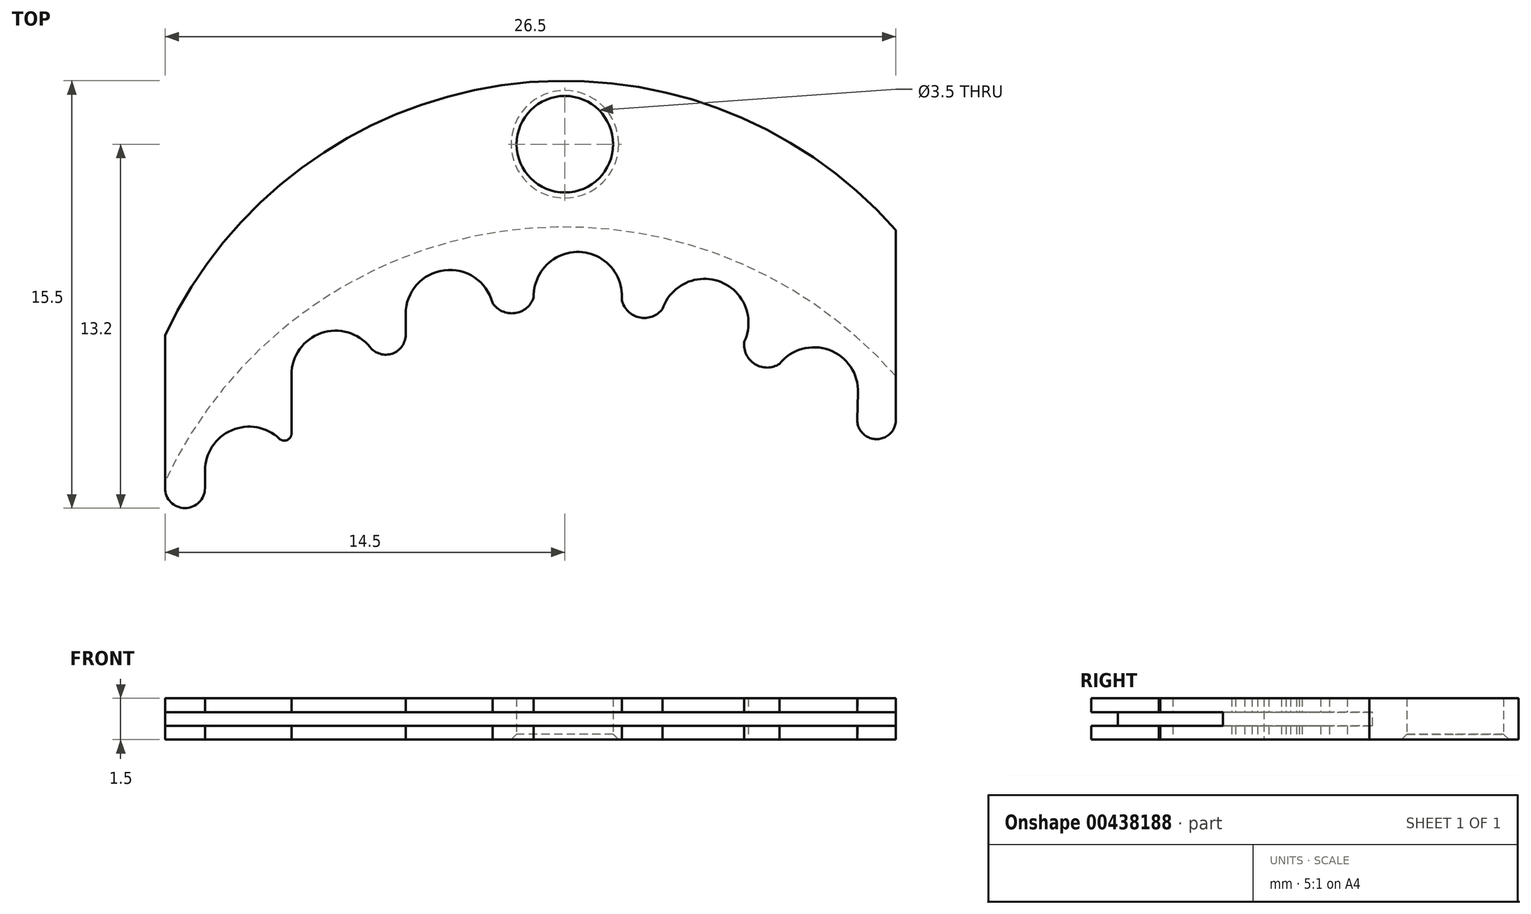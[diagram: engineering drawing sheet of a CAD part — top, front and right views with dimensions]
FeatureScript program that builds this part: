
annotation { "Feature Type Name" : "Feature", "Feature Type Description" : "" }
export const myFeature = defineFeature(function(context is Context, id is Id, definition is map)
    precondition{}
    {
        {
            var Q0;
            Q0=qCreatedBy(makeId("Top.planeOp"),FACE);
            var sketch = newSketch(context, id + "F0", { "sketchPlane" : qUnion([Q0])});
            skCircle(sketch, "E0", {"center": v(0, 0) * mm, "radius": 13 * mm, "construction": true});
            skCircle(sketch, "E1", {"center": v(0, 0) * mm, "radius": 13.5 * mm, "construction": true});
            skCircle(sketch, "E2", {"center": v(0, 0) * mm, "radius": 16 * mm, "construction": true});
            skLineSegment(sketch, "E3", {"start": v(0, 0) * mm, "end": v(0.47, 13.5) * mm, "construction": true});
            skLineSegment(sketch, "E4", {"start": v(0, 0) * mm, "end": v(5.06, 12.52) * mm, "construction": true});
            skLineSegment(sketch, "E5", {"start": v(0, 0) * mm, "end": v(9.03, 10.03) * mm, "construction": true});
            skLineSegment(sketch, "E6", {"start": v(0, 0) * mm, "end": v(-4.17, 12.84) * mm, "construction": true});
            skLineSegment(sketch, "E7", {"start": v(0, 0) * mm, "end": v(-8.31, 10.64) * mm, "construction": true});
            skLineSegment(sketch, "E8", {"start": v(0, 0) * mm, "end": v(-11.45, 7.15) * mm, "construction": true});
            skArc(sketch, "E9", {"start": v(2.06, 13.34) * mm, "mid": v(0.53, 15.1) * mm, "end": v(-1.13, 13.45) * mm});
            skArc(sketch, "E10", {"start": v(6.5, 11.83) * mm, "mid": v(5.66, 14) * mm, "end": v(3.54, 13.03) * mm});
            skArc(sketch, "E11", {"start": v(10.63, 9.98) * mm, "mid": v(9.59, 11.53) * mm, "end": v(7.78, 11.03) * mm});
            skArc(sketch, "E12", {"start": v(-2.62, 13.24) * mm, "mid": v(-4.38, 14.43) * mm, "end": v(-5.77, 12.84) * mm});
            skArc(sketch, "E13", {"start": v(-7, 11.55) * mm, "mid": v(-8.79, 12.17) * mm, "end": v(-9.91, 10.64) * mm});
            skArc(sketch, "E14", {"start": v(-10.35, 8.32) * mm, "mid": v(-12.08, 8.62) * mm, "end": v(-13.05, 7.15) * mm});
            skArc(sketch, "E15", {"start": v(-2.62, 13.24) * mm, "mid": v(-1.8, 12.87) * mm, "end": v(-1.13, 13.45) * mm});
            skArc(sketch, "E16", {"start": v(2.06, 13.34) * mm, "mid": v(2.7, 12.72) * mm, "end": v(3.54, 13.03) * mm});
            skArc(sketch, "E17", {"start": v(6.5, 11.83) * mm, "mid": v(6.89, 11.02) * mm, "end": v(7.78, 11.03) * mm});
            skLineSegment(sketch, "E18", {"start": v(-5.77, 12.84) * mm, "end": v(-5.77, 12.09) * mm});
            skLineSegment(sketch, "E19", {"start": v(-7.06, 11.64) * mm, "end": v(-7.06, 11.64) * mm});
            skArc(sketch, "E20", {"start": v(-7.06, 11.64) * mm, "mid": v(-6.26, 11.4) * mm, "end": v(-5.77, 12.09) * mm});
            skLineSegment(sketch, "E21", {"start": v(-9.91, 10.64) * mm, "end": v(-9.91, 8.5) * mm});
            skArc(sketch, "E22", {"start": v(-10.35, 8.32) * mm, "mid": v(-10.07, 8.27) * mm, "end": v(-9.91, 8.5) * mm});
            skArc(sketch, "E23", {"start": v(-14.5, 6.53) * mm, "mid": v(-13.77, 5.8) * mm, "end": v(-13.05, 6.53) * mm});
            skArc(sketch, "E24", {"start": v(10.6, 9.02) * mm, "mid": v(11.29, 8.3) * mm, "end": v(12, 9) * mm});
            skLineSegment(sketch, "E25", {"start": v(-14.5, 0) * mm, "end": v(-14.5, 12.06) * mm});
            skLineSegment(sketch, "E26", {"start": v(12, 0) * mm, "end": v(12, 15.88) * mm});
            skArc(sketch, "E27", {"start": v(12, 15.88) * mm, "mid": v(-2.28, 21.14) * mm, "end": v(-14.5, 12.06) * mm});
            skLineSegment(sketch, "E28", {"start": v(-13.05, 7.15) * mm, "end": v(-13.05, 6.53) * mm});
            skLineSegment(sketch, "E29", {"start": v(-14.5, 19) * mm, "end": v(12, 19) * mm, "construction": true});
            skLineSegment(sketch, "E30", {"start": v(10.63, 9.98) * mm, "end": v(10.6, 9.02) * mm});
            skCircle(sketch, "E31", {"center": v(0, 19) * mm, "radius": 1.75 * mm});
            skSolve(sketch);
        }
        {
            var Q0;
            Q0=makeQuery(id+"F0.imprint","IMPRINT",FACE,{"disambiguationData":[TD([[makeQuery(id+"F0.imprint","IMPRINT",EDGE,{"derivedFrom":sQuery(id+"F0.wireOp",EDGE,"E9")}),-1.0]])]});
            extrude(context, id + "F1", {"entities" : qUnion([Q0]), "endBound" : BoundingType.SYMMETRIC, "depth" : 1.5 * mm});
        }
        {
            var Q0;
            Q0=makeQuery(id+"F1.opExtrude","CAP_EDGE",EDGE,{"disambiguationData":[OSD([sQuery(id+"F0.wireOp",EDGE,"E31")])],"isStart":true});
            chamfer(context, id + "F2", {"entities" : qUnion([Q0]), "width" : 0.2 * mm, "tangentPropagation" : true});
        }
        {
            var Q0;
            Q0=qCreatedBy(makeId("Top.planeOp"),FACE);
            var sketch = newSketch(context, id + "F3", { "sketchPlane" : qUnion([Q0])});
            skCircle(sketch, "E32", {"center": v(0, 0) * mm, "radius": 16 * mm});
            skSolve(sketch);
        }
        {
            var Q0;
            Q0=makeQuery(id+"F3.imprint","IMPRINT",FACE,{"disambiguationData":[TD([[makeQuery(id+"F3.imprint","IMPRINT",EDGE,{"derivedFrom":sQuery(id+"F3.wireOp",EDGE,"E32")}),1.0]])]});
            extrude(context, id + "F4", {"entities" : qUnion([Q0]), "operationType" : NewBodyOperationType.REMOVE, "endBound" : BoundingType.SYMMETRIC, "oppositeDirection" : true, "depth" : 0.5 * mm});
        }
    });
